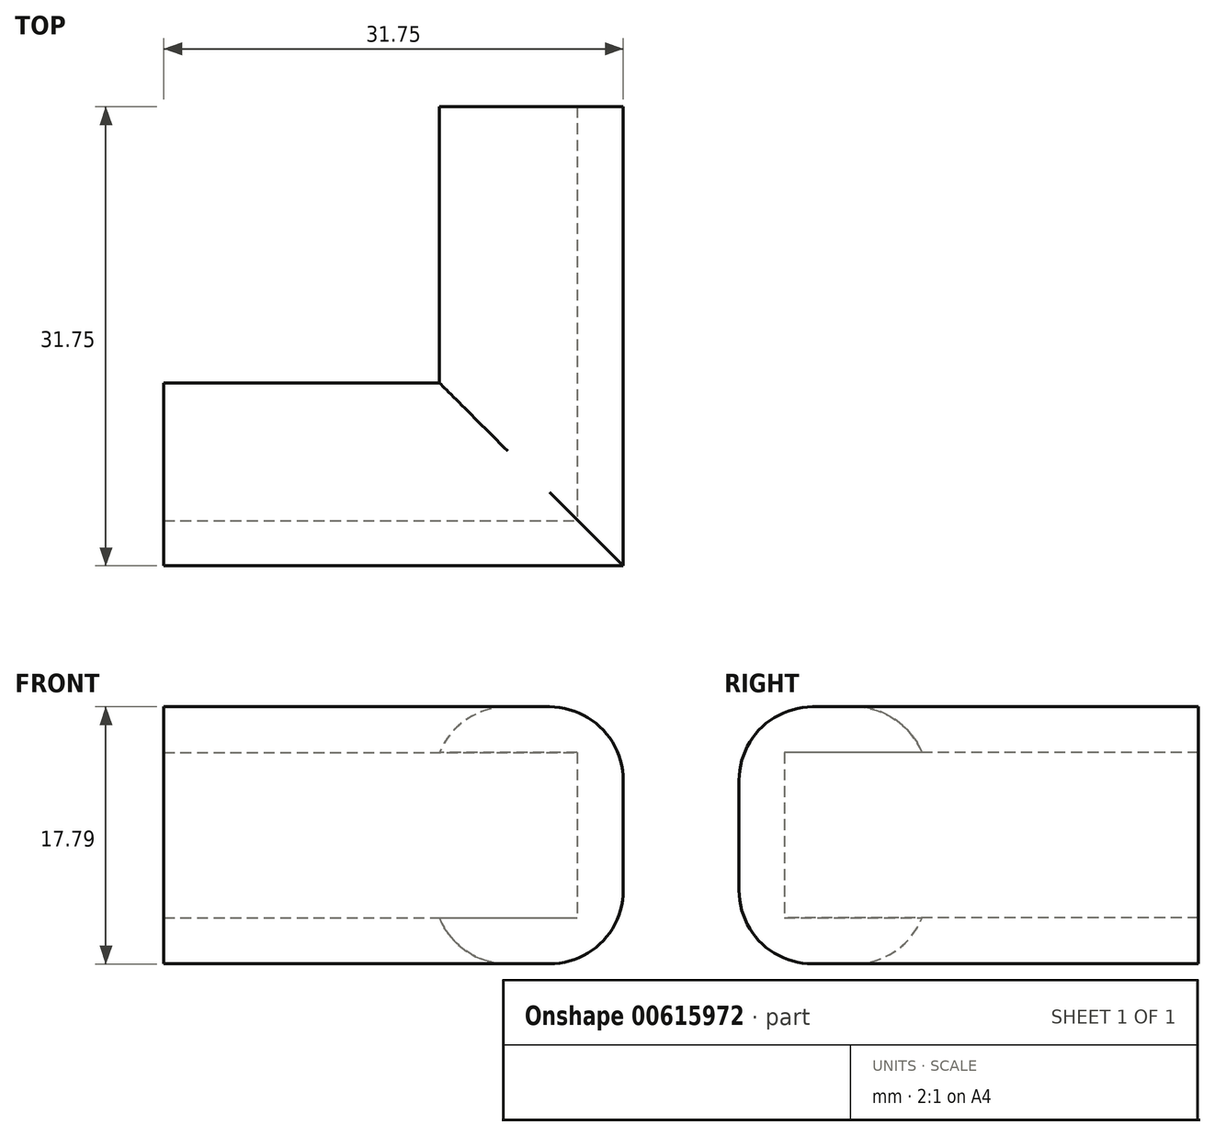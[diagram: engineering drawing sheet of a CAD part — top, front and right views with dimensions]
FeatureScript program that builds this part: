
annotation { "Feature Type Name" : "Feature", "Feature Type Description" : "" }
export const myFeature = defineFeature(function(context is Context, id is Id, definition is map)
    precondition{}
    {
        {
            var Q0;
            Q0=qCreatedBy(makeId("Front.planeOp"),FACE);
            var sketch = newSketch(context, id + "F0", { "sketchPlane" : qUnion([Q0])});
            skLineSegment(sketch, "E0", {"start": v(0, 8.26) * mm, "end": v(12.7, 8.26) * mm});
            skLineSegment(sketch, "E1", {"start": v(12.7, 8.26) * mm, "end": v(12.7, -9.52) * mm});
            skLineSegment(sketch, "E2", {"start": v(12.7, -9.52) * mm, "end": v(0, -9.52) * mm});
            skLineSegment(sketch, "E3", {"start": v(0, -9.52) * mm, "end": v(0, -6.35) * mm});
            skLineSegment(sketch, "E4", {"start": v(0, -6.35) * mm, "end": v(9.53, -6.35) * mm});
            skLineSegment(sketch, "E5", {"start": v(9.53, -6.35) * mm, "end": v(9.53, 5.08) * mm});
            skLineSegment(sketch, "E6", {"start": v(9.53, 5.08) * mm, "end": v(0, 5.08) * mm});
            skLineSegment(sketch, "E7", {"start": v(0, 5.08) * mm, "end": v(0, 8.26) * mm});
            skSolve(sketch);
        }
        {
            var Q0;
            Q0=qSketchRegion(id+"F0",true);
            extrude(context, id + "F1", {"entities" : qUnion([Q0]), "oppositeDirection" : true, "depth" : 31.75 * mm});
        }
        {
            var Q0;
            Q0=makeQuery(id+"F1.opExtrude","SWEPT_FACE",FACE,{"disambiguationData":[OSD([sQuery(id+"F0.wireOp",EDGE,"E1")])]});
            var sketch = newSketch(context, id + "F2", { "sketchPlane" : qUnion([Q0])});
            skLineSegment(sketch, "E8", {"start": v(12.7, -9.52) * mm, "end": v(0, -9.52) * mm});
            skLineSegment(sketch, "E9", {"start": v(0, -9.52) * mm, "end": v(0, 8.26) * mm});
            skLineSegment(sketch, "E10", {"start": v(0, 8.26) * mm, "end": v(12.65, 8.26) * mm});
            skLineSegment(sketch, "E11", {"start": v(12.65, 8.26) * mm, "end": v(12.65, 5.08) * mm});
            skLineSegment(sketch, "E12", {"start": v(12.65, 5.08) * mm, "end": v(3.12, 5.08) * mm});
            skLineSegment(sketch, "E13", {"start": v(3.12, 5.08) * mm, "end": v(3.12, -6.35) * mm});
            skLineSegment(sketch, "E14", {"start": v(3.12, -6.35) * mm, "end": v(12.65, -6.35) * mm});
            skLineSegment(sketch, "E15", {"start": v(12.65, -6.35) * mm, "end": v(12.7, -9.52) * mm});
            skSolve(sketch);
        }
        {
            var Q0;
            Q0=qSketchRegion(id+"F2",true);
            extrude(context, id + "F3", {"entities" : qUnion([Q0]), "operationType" : NewBodyOperationType.ADD, "oppositeDirection" : true, "depth" : 31.75 * mm});
        }
        {
            var Q0;
            Q0=makeQuery(id+"F3.opExtrude","SWEPT_EDGE",EDGE,{"disambiguationData":[OSD([sQuery(id+"F2.wireOp",EDGE,"E9"),sQuery(id+"F2.wireOp",EDGE,"E10")])]});
            var Q1;
            Q1=makeQuery(id+"F1.opExtrude","SWEPT_EDGE",EDGE,{"disambiguationData":[OSD([sQuery(id+"F0.wireOp",EDGE,"E0"),sQuery(id+"F0.wireOp",EDGE,"E1")])]});
            var Q2;
            Q2=makeQuery(id+"F1.opExtrude","SWEPT_EDGE",EDGE,{"disambiguationData":[OSD([sQuery(id+"F0.wireOp",EDGE,"E1"),sQuery(id+"F0.wireOp",EDGE,"E2")])]});
            var Q3;
            Q3=makeQuery(id+"F1.opExtrude","SWEPT_EDGE",EDGE,{"disambiguationData":[OSD([sQuery(id+"F0.wireOp",EDGE,"E0"),sQuery(id+"F0.wireOp",EDGE,"E7")])]});
            var Q4;
            Q4=makeQuery(id+"F3.opExtrude","SWEPT_EDGE",EDGE,{"disambiguationData":[OSD([sQuery(id+"F0.wireOp",EDGE,"E0"),sQuery(id+"F0.wireOp",EDGE,"E1"),sQuery(id+"F2.wireOp",EDGE,"E10"),sQuery(id+"F2.wireOp",EDGE,"E11")])]});
            var Q5;
            Q5=makeQuery(id+"F3.opExtrude","SWEPT_EDGE",EDGE,{"disambiguationData":[OSD([sQuery(id+"F0.wireOp",EDGE,"E1"),sQuery(id+"F0.wireOp",EDGE,"E2"),sQuery(id+"F2.wireOp",EDGE,"E8"),sQuery(id+"F2.wireOp",EDGE,"E15")])]});
            var Q6;
            Q6=makeQuery(id+"F1.opExtrude","SWEPT_EDGE",EDGE,{"disambiguationData":[OSD([sQuery(id+"F0.wireOp",EDGE,"E2"),sQuery(id+"F0.wireOp",EDGE,"E3")])]});
            var Q7;
            Q7=makeQuery(id+"F3.boolean.opBoolean","MERGE",EDGE,{"derivedFrom":[makeQuery(id+"F1.opExtrude","CAP_EDGE",EDGE,{"disambiguationData":[OSD([sQuery(id+"F0.wireOp",EDGE,"E2")])],"isStart":true}),makeQuery(id+"F3.opExtrude","SWEPT_EDGE",EDGE,{"disambiguationData":[OSD([sQuery(id+"F2.wireOp",EDGE,"E8"),sQuery(id+"F2.wireOp",EDGE,"E9")])]})]});
            var Q8;
            Q8=makeQuery(id+"F3.opExtrude","SWEPT_EDGE",EDGE,{"disambiguationData":[OSD([sQuery(id+"F2.wireOp",EDGE,"E13"),sQuery(id+"F2.wireOp",EDGE,"E14")])]});
            fillet(context, id + "F4", {"entities" : qUnion([Q0, Q1, Q2, Q3, Q4, Q5, Q6, Q7, Q8]), "radius" : 5.08 * mm, "tangentPropagation" : true, "allowEdgeOverflow" : false});
        }
    });
